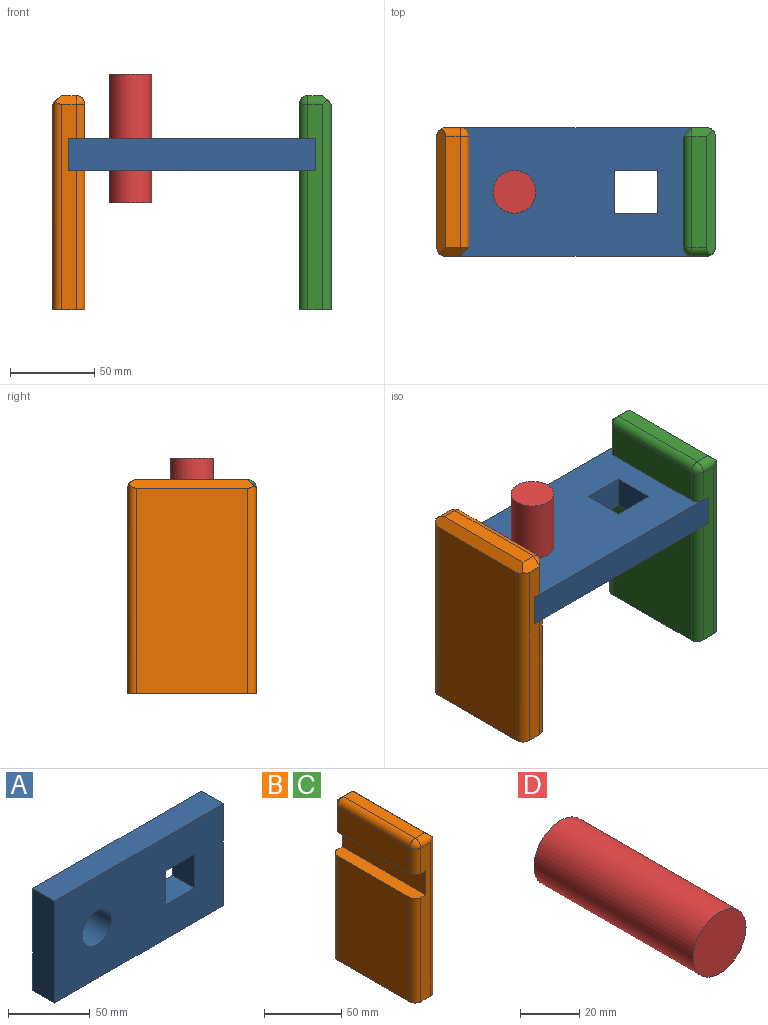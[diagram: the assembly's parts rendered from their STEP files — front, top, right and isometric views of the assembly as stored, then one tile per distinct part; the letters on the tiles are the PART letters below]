
ASSEMBLY  parts=4 mates=3
PART A: 11 faces, bbox 146.1x19.1x76.2 mm
  f0: plane 76.2x19.05mm, normal (1,0,0), area 1451.6mm2, adj f1,f8,f9,f10
  f1: plane 146.05x19.05mm, normal (0,0,1), area 2782.3mm2, adj f0,f2,f9,f10
  f2: plane 76.2x19.05mm, normal (-1,0,0), area 1451.6mm2, adj f1,f8,f9,f10
  f3: plane 25.4x19.05mm, normal (0,0,1), area 483.9mm2, adj f4,f6,f9,f10
  f4: plane 25.4x19.05mm, normal (1,0,0), area 483.9mm2, adj f3,f5,f9,f10
  f5: plane 25.4x19.05mm, normal (0,0,-1), area 483.9mm2, adj f4,f6,f9,f10
  f6: plane 25.4x19.05mm, normal (-1,0,0), area 483.9mm2, adj f3,f5,f9,f10
  f7: cylinder r=12.7mm len=25.4mm, axis (0,1,0), area 1520.1mm2, adj f9,f10
  f8: plane 146.05x19.05mm, normal (0,0,-1), area 2782.3mm2, adj f0,f2,f9,f10
  f9: plane 146.05x76.2mm, normal (0,-1,0), area 9977.1mm2, adj f0,f1,f2,f3,f4,f5,f6,f7
  f10: plane 146.05x76.2mm, normal (0,1,0), area 9977.1mm2, adj f0,f1,f2,f3,f4,f5,f6,f7
PART B: 22 faces, bbox 19.1x76.2x127 mm
  f0: plane 82.55x66.04mm, normal (-1,0,0), area 5451.6mm2, adj f1,f7,f19,f21
  f1: plane 76.2x19.05mm, normal (0,0,-1), area 1429.5mm2, adj f0,f2,f8,f9,f18,f19,f20,f21
  f2: plane 121.92x66.04mm, normal (1,0,0), area 8051.6mm2, adj f1,f10,f18,f20
  f3: plane 66.04x8.89mm, normal (0,0,1), area 587.1mm2, adj f10,f11,f12,f15
  f4: plane 66.04x20.32mm, normal (-1,0,0), area 1341.9mm2, adj f5,f11,f14,f17
  f5: plane 76.2x9.53mm, normal (0,0,-1), area 707.4mm2, adj f4,f6,f8,f9,f14,f17
  f6: plane 76.2x19.05mm, normal (-1,0,0), area 1451.6mm2, adj f5,f7,f8,f9
  f7: plane 76.2x9.53mm, normal (0,0,1), area 714.7mm2, adj f0,f6,f8,f9,f19,f21
  f8: plane 121.92x8.89mm, normal (0,-1,0), area 999.2mm2, adj f1,f5,f6,f7,f12,f14,f20,f21
  f9: plane 121.92x8.89mm, normal (0,1,0), area 999.2mm2, adj f1,f5,f6,f7,f15,f17,f18,f19
  f10: plane 74.03x5.08mm, normal (0.71,0,0.71), area 511.2mm2, adj f2,f3,f12,f15,f18,f20
  f11: cylinder r=5.08mm len=66.04mm, axis (0,1,0), area 527mm2, adj f3,f4,f13,f16
  f12: cylinder r=5.08mm len=11.43mm, axis (1,0,0), area 79.1mm2, adj f3,f8,f10,f13,f20
  f13: sphere r=5.08mm, area 40.5mm2, adj f11,f12,f14
  f14: cylinder r=5.08mm len=20.32mm, axis (0,0,1), area 162.1mm2, adj f4,f5,f8,f13
  f15: plane 12.48x5.08mm, normal (0,0.71,0.71), area 78.2mm2, adj f3,f9,f10,f16,f18
  f16: cone r=5.08mm half-angle=45deg, axis (0,-1,0), area 28.7mm2, adj f11,f15,f17
  f17: plane 20.32x5.08mm, normal (-0.71,0.71,0), area 146mm2, adj f4,f5,f9,f16
  f18: cylinder r=5.08mm len=123.41mm, axis (0,0,1), area 976.9mm2, adj f1,f2,f9,f10,f15
  f19: cylinder r=5.08mm len=82.55mm, axis (0,0,-1), area 658.7mm2, adj f0,f1,f7,f9
  f20: cylinder r=5.08mm len=124.46mm, axis (0,0,-1), area 981mm2, adj f1,f2,f8,f10,f12
  f21: cylinder r=5.08mm len=82.55mm, axis (0,0,1), area 658.7mm2, adj f0,f1,f7,f8
PART C: same geometry as B
PART D: 3 faces, bbox 25.4x76.2x25.4 mm
  f0: cylinder r=12.7mm len=76.2mm, axis (0,1,0), area 6080.5mm2, adj f1,f2
  f1: plane 25.4x25.4mm, normal (0,-1,0), area 506.7mm2, adj f0
  f2: plane 25.4x25.4mm, normal (0,1,0), area 506.7mm2, adj f0
PLACE A rot(axis=(1,0,0),90deg) t=(-6.71,43.22,91.44)mm
PLACE B rot(axis=(0,0,1),180deg) t=(-162.29,-32.98,-10.16)mm
PLACE C t=(2.81,43.22,-10.16)mm
PLACE D rot(axis=(1,0,0),90deg) t=(-111.87,11.46,129.54)mm
MATE slider D.f0 <-> A.f7  axis (0,0,1) through (-116.25,5.12,91.44)mm
MATE planar C.f6 <-> A.f0  axis (-1,0,0) through (-6.71,5.12,81.91)mm
MATE planar B.f6 <-> A.f2  axis (1,0,0) through (-152.76,5.12,81.91)mm
